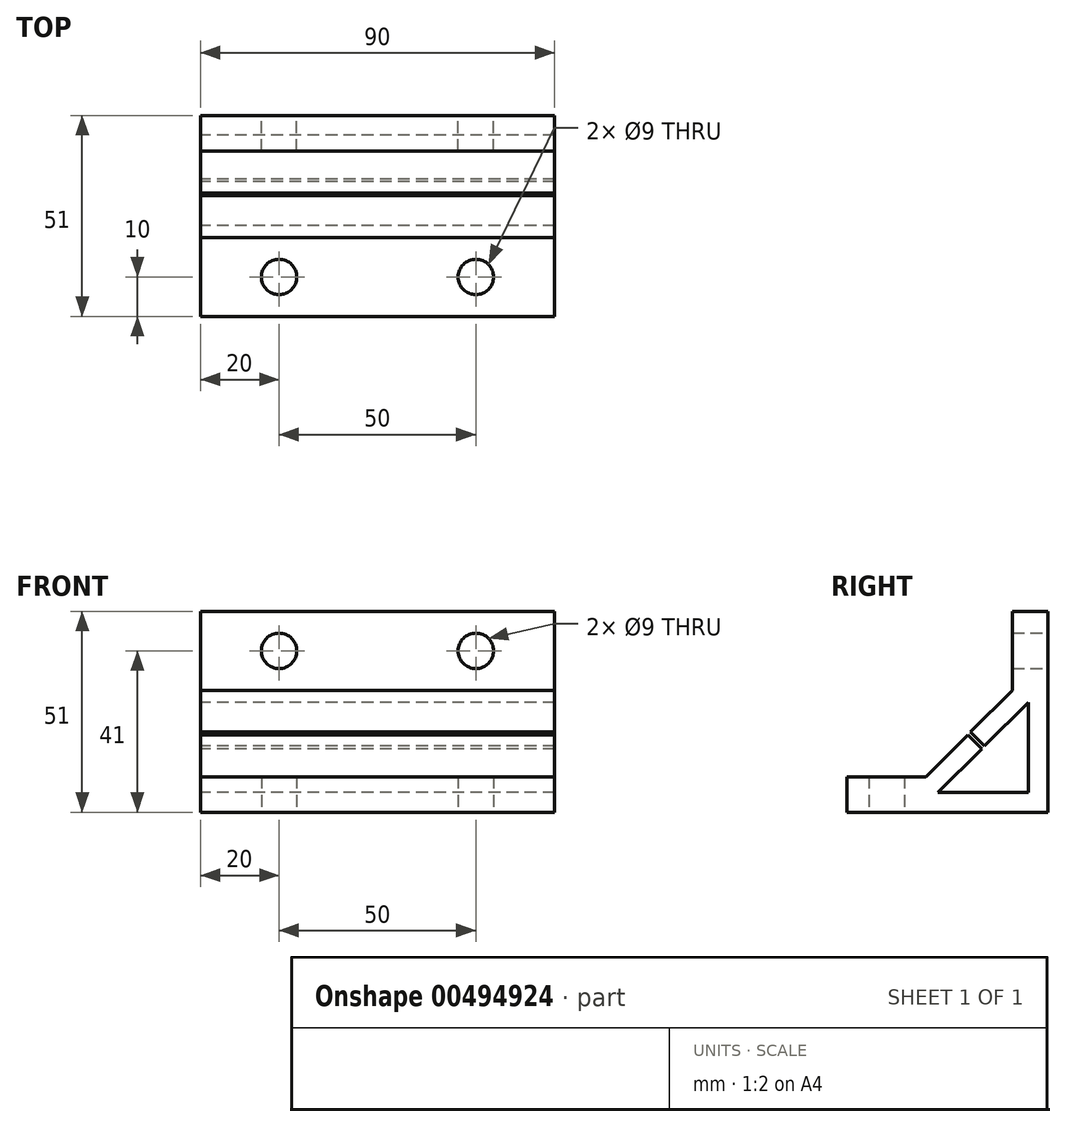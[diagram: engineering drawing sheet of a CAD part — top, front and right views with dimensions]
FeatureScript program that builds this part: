
annotation { "Feature Type Name" : "Feature", "Feature Type Description" : "" }
export const myFeature = defineFeature(function(context is Context, id is Id, definition is map)
    precondition{}
    {
        {
            var Q0;
            Q0=qCreatedBy(makeId("Right.planeOp"),FACE);
            var sketch = newSketch(context, id + "F0", { "sketchPlane" : qUnion([Q0])});
            skLineSegment(sketch, "E0", {"start": v(0, 0) * mm, "end": v(0, 51) * mm});
            skLineSegment(sketch, "E1", {"start": v(0, 51) * mm, "end": v(-9, 51) * mm});
            skLineSegment(sketch, "E2", {"start": v(-9, 51) * mm, "end": v(-9, 31) * mm});
            skLineSegment(sketch, "E3", {"start": v(-9, 31) * mm, "end": v(-19.65, 20.35) * mm});
            skLineSegment(sketch, "E4", {"start": v(-31, 9) * mm, "end": v(-51, 9) * mm});
            skLineSegment(sketch, "E5", {"start": v(-51, 9) * mm, "end": v(-51, 0) * mm});
            skLineSegment(sketch, "E6", {"start": v(-51, 0) * mm, "end": v(0, 0) * mm});
            skLineSegment(sketch, "E7", {"start": v(-5, 27.93) * mm, "end": v(-16.11, 16.82) * mm});
            skLineSegment(sketch, "E8", {"start": v(-27.93, 5) * mm, "end": v(-5, 5) * mm});
            skLineSegment(sketch, "E9", {"start": v(-5, 5) * mm, "end": v(-5, 27.93) * mm});
            skLineSegment(sketch, "E10", {"start": v(-19.65, 20.35) * mm, "end": v(-16.11, 16.82) * mm});
            skLineSegment(sketch, "E11", {"start": v(-20.35, 19.65) * mm, "end": v(-16.82, 16.11) * mm});
            skPoint(sketch, "E12.end.orphan", {"position": v(-16.46, 16.46) * mm});
            skPoint(sketch, "E12.start.orphan", {"position": v(-20, 20) * mm});
            skLineSegment(sketch, "E13.trimOffspring", {"start": v(-20.35, 19.65) * mm, "end": v(-31, 9) * mm});
            skLineSegment(sketch, "E14.trimOffspring", {"start": v(-16.82, 16.11) * mm, "end": v(-27.93, 5) * mm});
            skSolve(sketch);
        }
        {
            var Q0;
            Q0=qSketchRegion(id+"F0",true);
            extrude(context, id + "F1", {"entities" : qUnion([Q0]), "depth" : 90 * mm});
        }
        {
            var Q0;
            Q0=makeQuery(id+"F1.opExtrude","SWEPT_FACE",FACE,{"disambiguationData":[OSD([sQuery(id+"F0.wireOp",EDGE,"E0")])]});
            var sketch = newSketch(context, id + "F2", { "sketchPlane" : qUnion([Q0])});
            skPoint(sketch, "E15", {"position": v(-20, 41) * mm});
            skPoint(sketch, "E16", {"position": v(-70, 41) * mm});
            skSolve(sketch);
        }
        {
            var Q0;
            Q0=makeQuery(id+"F1.opExtrude","SWEPT_FACE",FACE,{"disambiguationData":[OSD([sQuery(id+"F0.wireOp",EDGE,"E6")])]});
            var sketch = newSketch(context, id + "F3", { "sketchPlane" : qUnion([Q0])});
            skPoint(sketch, "E17", {"position": v(20, 41) * mm});
            skPoint(sketch, "E18", {"position": v(70, 41) * mm});
            skSolve(sketch);
        }
        {
            var Q0;
            Q0=sQuery(id+"F3.wireOp",VERTEX,"E18");
            var Q1;
            Q1=sQuery(id+"F3.wireOp",VERTEX,"E17");
            var Q2;
            Q2=sQuery(id+"F2.wireOp",VERTEX,"E15");
            var Q3;
            Q3=sQuery(id+"F2.wireOp",VERTEX,"E16");
            var Q4;
            Q4=makeQuery(id+"F1.opExtrude","SWEPT_BODY",BODY,{"disambiguationData":[OSD([sQuery(id+"F0.wireOp",EDGE,"E0"),sQuery(id+"F0.wireOp",EDGE,"E1"),sQuery(id+"F0.wireOp",EDGE,"E2"),sQuery(id+"F0.wireOp",EDGE,"E3"),sQuery(id+"F0.wireOp",EDGE,"E4"),sQuery(id+"F0.wireOp",EDGE,"E5"),sQuery(id+"F0.wireOp",EDGE,"E6"),sQuery(id+"F0.wireOp",EDGE,"E7"),sQuery(id+"F0.wireOp",EDGE,"E8"),sQuery(id+"F0.wireOp",EDGE,"E9"),sQuery(id+"F0.wireOp",EDGE,"E10"),sQuery(id+"F0.wireOp",EDGE,"E11"),sQuery(id+"F0.wireOp",EDGE,"E13.trimOffspring"),sQuery(id+"F0.wireOp",EDGE,"E14.trimOffspring")])]});
            hole(context, id + "F4", {"style" : HoleStyle.SIMPLE, "endStyle" : HoleEndStyle.THROUGH, "holeDiameter" : 9 * mm, "isTappedThrough" : true, "tappedDepth" : 7.9 * mm, "tapClearance" : 3, "locations" : qUnion([Q0, Q1, Q2, Q3]), "scope" : qUnion([Q4])});
        }
    });
